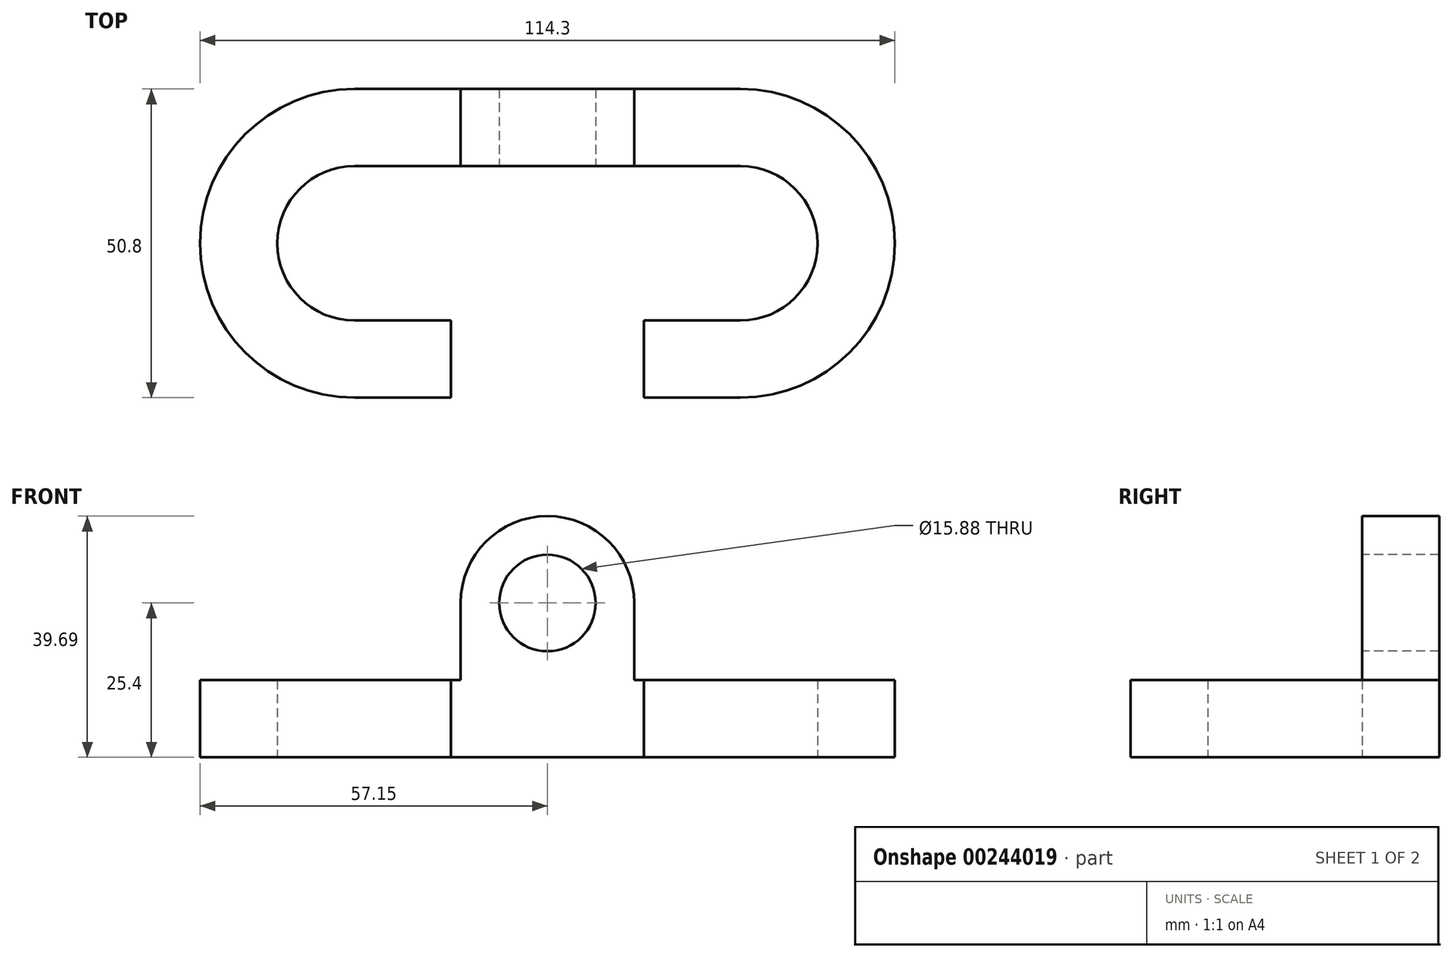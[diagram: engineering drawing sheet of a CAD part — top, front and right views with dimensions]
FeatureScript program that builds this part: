
annotation { "Feature Type Name" : "Feature", "Feature Type Description" : "" }
export const myFeature = defineFeature(function(context is Context, id is Id, definition is map)
    precondition{}
    {
        {
            var Q0;
            Q0=qCreatedBy(makeId("Top.planeOp"),FACE);
            var sketch = newSketch(context, id + "F0", { "sketchPlane" : qUnion([Q0])});
            skArc(sketch, "E0", {"start": v(31.75, -12.7) * mm, "mid": v(44.45, 0) * mm, "end": v(31.75, 12.7) * mm});
            skArc(sketch, "E1", {"start": v(31.75, -25.4) * mm, "mid": v(57.15, 0) * mm, "end": v(31.75, 25.4) * mm});
            skLineSegment(sketch, "E2", {"start": v(31.75, 25.4) * mm, "end": v(0, 25.4) * mm});
            skLineSegment(sketch, "E3", {"start": v(31.75, 12.7) * mm, "end": v(0, 12.7) * mm});
            skLineSegment(sketch, "E4", {"start": v(31.75, -25.4) * mm, "end": v(15.88, -25.4) * mm});
            skLineSegment(sketch, "E5", {"start": v(31.75, -12.7) * mm, "end": v(15.88, -12.7) * mm});
            skLineSegment(sketch, "E6", {"start": v(15.88, -12.7) * mm, "end": v(15.88, -25.4) * mm});
            skLineSegment(sketch, "E7.MirrorCS", {"start": v(-31.75, 25.4) * mm, "end": v(0, 25.4) * mm});
            skArc(sketch, "E8.MirrorCS", {"start": v(-31.75, -25.4) * mm, "mid": v(-57.15, 0) * mm, "end": v(-31.75, 25.4) * mm});
            skArc(sketch, "E9.MirrorCS", {"start": v(-31.75, -12.7) * mm, "mid": v(-44.45, 0) * mm, "end": v(-31.75, 12.7) * mm});
            skLineSegment(sketch, "E10.MirrorCS", {"start": v(-31.75, 12.7) * mm, "end": v(0, 12.7) * mm});
            skLineSegment(sketch, "E11.MirrorCS", {"start": v(-31.75, -12.7) * mm, "end": v(-15.88, -12.7) * mm});
            skLineSegment(sketch, "E12.MirrorCS", {"start": v(-15.88, -12.7) * mm, "end": v(-15.88, -25.4) * mm});
            skLineSegment(sketch, "E13.MirrorCS", {"start": v(-31.75, -25.4) * mm, "end": v(-15.88, -25.4) * mm});
            skSolve(sketch);
        }
        {
            var Q0;
            Q0 = qSketchRegion(id + "F0", true);
            extrude(context, id + "F1", {"entities" : qUnion([Q0]), "depth" : 12.7 * mm});
        }
        {
            var Q0;
            Q0=makeQuery(id+"F1.opExtrude","SWEPT_FACE",FACE,{"disambiguationData":[OSD([sQuery(id+"F0.wireOp",EDGE,"E3"),sQuery(id+"F0.wireOp",EDGE,"E10.MirrorCS")])]});
            var sketch = newSketch(context, id + "F2", { "sketchPlane" : qUnion([Q0])});
            skCircle(sketch, "E14", {"center": v(0, 25.4) * mm, "radius": 7.94 * mm});
            skArc(sketch, "E15", {"start": v(14.29, 25.4) * mm, "mid": v(0, 39.69) * mm, "end": v(-14.29, 25.4) * mm});
            skLineSegment(sketch, "E16", {"start": v(-14.29, 25.4) * mm, "end": v(-14.29, 12.7) * mm});
            skLineSegment(sketch, "E17", {"start": v(14.29, 25.4) * mm, "end": v(14.29, 12.7) * mm});
            skLineSegment(sketch, "E18", {"start": v(-14.29, 12.7) * mm, "end": v(14.29, 12.7) * mm});
            skSolve(sketch);
        }
        {
            var Q0;
            Q0 = qSketchRegion(id + "F2", true);
            extrude(context, id + "F3", {"entities" : qUnion([Q0]), "operationType" : NewBodyOperationType.ADD, "oppositeDirection" : true, "depth" : 12.7 * mm});
        }
    });
